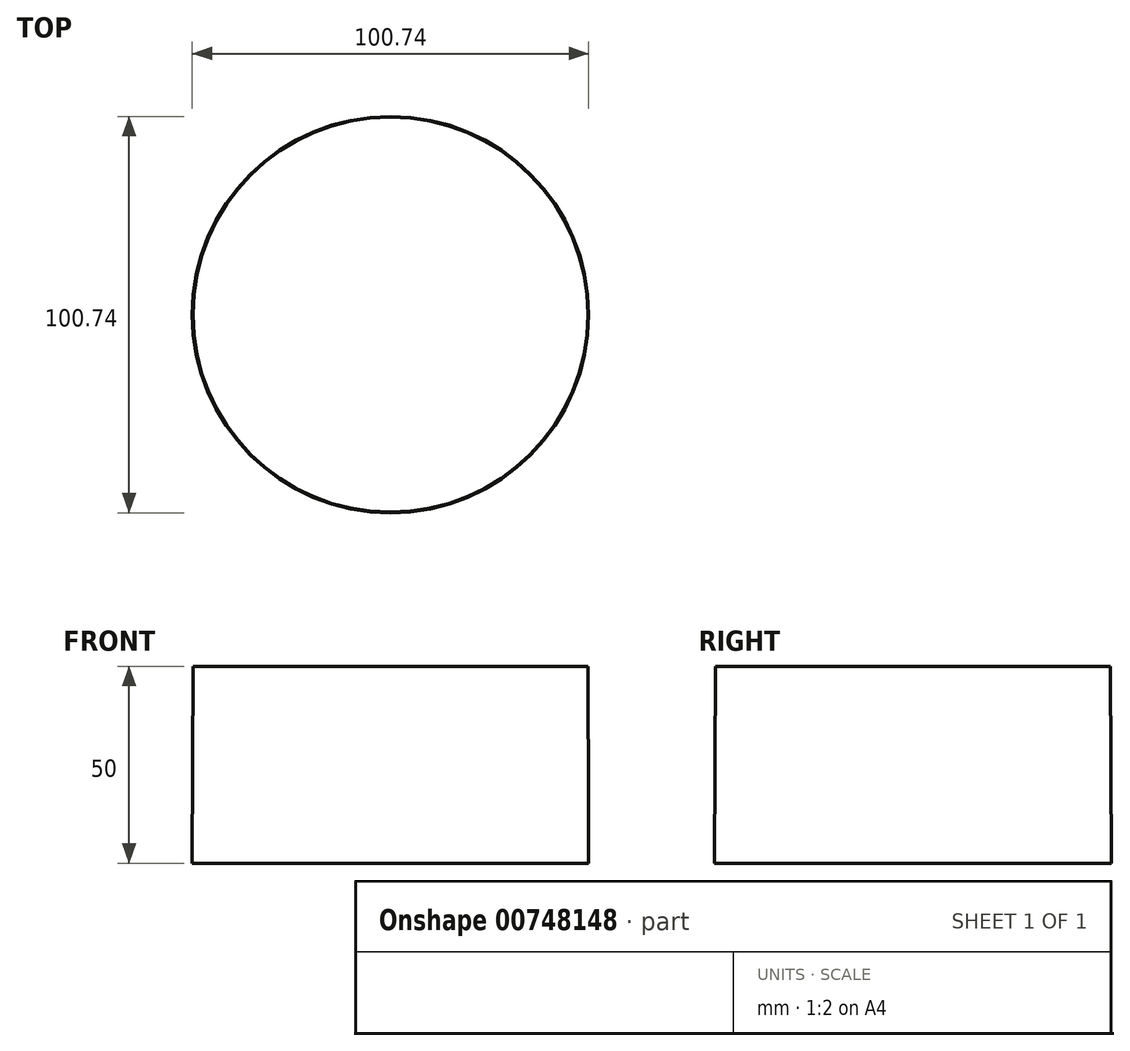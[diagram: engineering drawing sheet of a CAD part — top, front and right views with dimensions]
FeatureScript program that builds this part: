
annotation { "Feature Type Name" : "Feature", "Feature Type Description" : "" }
export const myFeature = defineFeature(function(context is Context, id is Id, definition is map)
    precondition{}
    {
        {
            var Q0;
            Q0=qCreatedBy(makeId("Top.planeOp"),FACE);
            cPlane(context, id + "F0", {"entities" : qUnion([Q0]), "cplaneType" : CPlaneType.OFFSET, "offset" : 50 * mm, "width" : 150 * mm, "height" : 150 * mm});
        }
        {
            var Q0;
            Q0=qCreatedBy(id+"F0.planeOp",FACE);
            var sketch = newSketch(context, id + "F1", { "sketchPlane" : qUnion([Q0])});
            skCircle(sketch, "E0", {"center": v(0, 0) * mm, "radius": 50.19 * mm});
            skSolve(sketch);
        }
        {
            var Q0;
            Q0=qCreatedBy(makeId("Top.planeOp"),FACE);
            var sketch = newSketch(context, id + "F2", { "sketchPlane" : qUnion([Q0])});
            skCircle(sketch, "E1", {"center": v(0, 0) * mm, "radius": 50.37 * mm});
            skSolve(sketch);
        }
        {
            var Q0;
            Q0=makeQuery(id+"F1.imprint","IMPRINT",FACE,{"disambiguationData":[TD([[makeQuery(id+"F1.imprint","IMPRINT",EDGE,{"derivedFrom":sQuery(id+"F1.wireOp",EDGE,"E0")}),1.0]])]});
            var Q1;
            Q1=makeQuery(id+"F2.imprint","IMPRINT",FACE,{"disambiguationData":[TD([[makeQuery(id+"F2.imprint","IMPRINT",EDGE,{"derivedFrom":sQuery(id+"F2.wireOp",EDGE,"E1")}),1.0]])]});
            loft(context, id + "F3", {"sheetProfilesArray" : [{ "sheetProfileEntities" : qUnion([Q0]) }, { "sheetProfileEntities" : qUnion([Q1]) }]});
        }
    });
